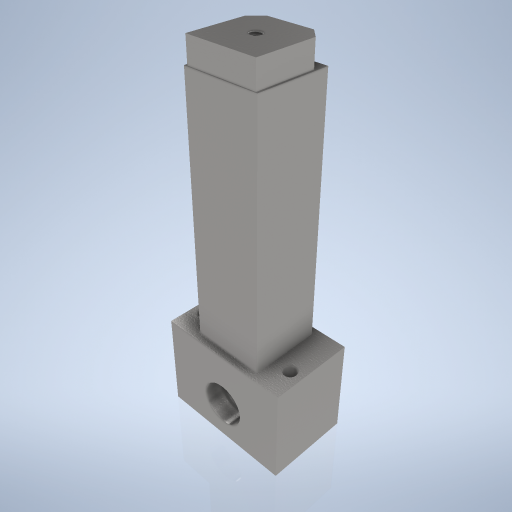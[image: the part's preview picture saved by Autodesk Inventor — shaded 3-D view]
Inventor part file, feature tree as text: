
AUTODESK INVENTOR PART (.ipt)
format: ipt  version: 2024.2 (Build 282272000, 272)  size: 322,560 bytes
history: native  units: mm
features: sketch x6, extrude x3, hole x3, chamfer x1, mirror x1
ambient origin geometry x8: Origin, YZ Plane, XZ Plane, XY Plane, X Axis, Y Axis, Z Axis, Center Point
bodies: Volumenkörper1 (feature_tree)
feature tree (14):
  extrude  "Extrusion1"  Depth=19.0mm
  extrude  "Extrusion3"  Depth=16.0mm
  chamfer  "Fasen1"  Distance=55.0mm
  extrude  "Extrusion2"  Depth=2.0mm
  hole  "Bohrung1"  [1 undecoded]
  hole  "Bohrung2"  [1 undecoded]
  mirror  "Spiegeln1"
  hole  "Bohrung3"  [1 undecoded]
  sketch  "Skizze1"  dims[d0=30.0mm d1=19.0mm]
  sketch  "Skizze2"  dims[d2=22.0mm d3=0.0mm d4=16.0mm d5=55.0mm d6=0.0mm]
  sketch  "Skizze3"  dims[d7=15.5mm]
  sketch  "Skizze4"  dims[d8=2.459mm d9=12.0mm d10=4.0mm d11=2.0mm d12=90.0deg d13=15.0mm d14=20.594885mm]
  sketch  "Skizze5"  dims[d15=7.5mm d16=12.0mm d17=10.0mm d18=4.0mm d19=90.0deg d20=9.5mm d21=0.0mm]
  sketch  "Skizze7"  dims[d23=3.1mm d24=6.0mm d25=10.0mm d26=4.0mm d27=90.0deg d28=9.5mm d29=0.0mm d30=24.0mm d31=12.0mm d34=6.5mm d35=6.5mm d36=15.0mm d37=15.0mm d38=60.0mm d39=0.0mm d40=2.5mm d41=2.0mm d42=45.0deg d43=73.0mm]
note: 3 required parameter values undecoded (feature->parameter linkage not recoverable at this tier; creation-order binding heuristic only, values carry confidence <= 0.55)
